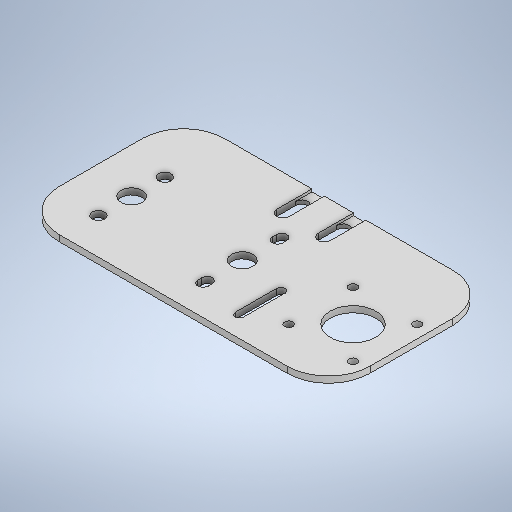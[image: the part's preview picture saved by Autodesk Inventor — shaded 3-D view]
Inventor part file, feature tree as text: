
AUTODESK INVENTOR PART (.ipt)
format: ipt  version: 2025.2 (Build 292293000, 293)  size: 354,304 bytes
history: native  units: mm
features: extrude x6, sketch x5, fillet x1
ambient origin geometry x8: Origin, YZ Plane, XZ Plane, XY Plane, X Axis, Y Axis, Z Axis, Center Point
bodies: Solid1 (feature_tree)
feature tree (12):
  extrude  "Extrusion1"  Depth=80.0mm
  sketch  "Sketch4"  dims[d2=3.0mm d3=0.0mm d14=20.0mm]
  extrude  "Extrusion3"  Depth=20.0mm
  extrude  "Extrusion4"  Depth=6.0mm
  extrude  "Extrusion5"  Depth=5.0mm
  extrude  "Extrusion6"  Depth=3.0mm
  fillet  "Fillet1"  Radius=3.0mm
  extrude  "Extrusion7"  Depth=3.0mm
  sketch  "Sketch1"  dims[d0=150.0mm d1=80.0mm]
  sketch  "Sketch5"  dims[d15=20.0mm d16=6.0mm]
  sketch  "Sketch6"  dims[d17=6.0mm d18=5.0mm]
  sketch  "Sketch7"  dims[d19=5.0mm d20=3.0mm d21=3.0mm d22=3.0mm d23=3.0mm d24=0.0mm d25=0.0mm d26=25.0mm d36=0.0mm d37=0.0mm d38=1.2mm d39=0.0mm d49=150.0mm d50=43.2mm d51=43.2mm d52=22.0mm d53=31.0mm d54=31.0mm d55=4.0mm d56=4.0mm d57=4.0mm d58=4.0mm d59=25.0mm d60=43.2mm d61=43.2mm d62=43.2mm d63=10.2mm d64=43.2mm d65=53.4mm d66=10.2mm d67=0.0mm d68=0.0mm d69=38.0mm d70=5.0mm d71=2.0mm d72=5.0mm d73=5.0mm d74=2.0mm d75=5.0mm d84=32.0mm d85=6.0mm d86=6.0mm d87=20.0mm d88=22.0mm d89=30.0mm d90=4.0mm d91=20.0mm d92=0.0mm d93=0.0mm d27=0.872665mm d28=0.5mm d29=0.872665mm]
